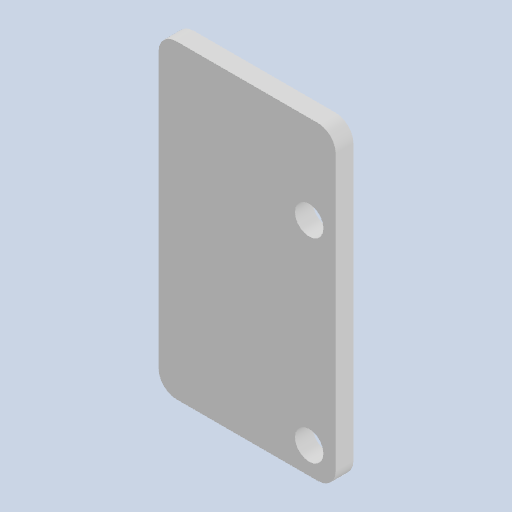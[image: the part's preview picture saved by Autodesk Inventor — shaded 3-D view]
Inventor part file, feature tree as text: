
AUTODESK INVENTOR PART (.ipt)
format: ipt  version: 2022 (Build 260153000, 153)  size: 109,056 bytes
history: native  units: mm
features: other x4, extrude x2, sketch x2, fillet x1, reference x1
ambient origin geometry x8: Origin, YZ Plane, XZ Plane, XY Plane, X Axis, Y Axis, Z Axis, Center Point
bodies: Body1 (feature_tree)
feature tree (10):
  other  "Твердое тело1"
  extrude  "Выдавливание1"  Depth=20.0mm
  fillet  "Сопряжение1"  Radius=35.0mm
  extrude  "Выдавливание2"  Depth=2.0mm TaperAngle=0.0deg
  sketch  "Эскиз1"
  sketch  "Эскиз2"
  reference  "Ссылка1"
  other  "<userpath>\Documents\Git\MZCAT_2024\MZCAT_3.iam"
  other  "MZCAT_3.iam"
  other  "base:1"
